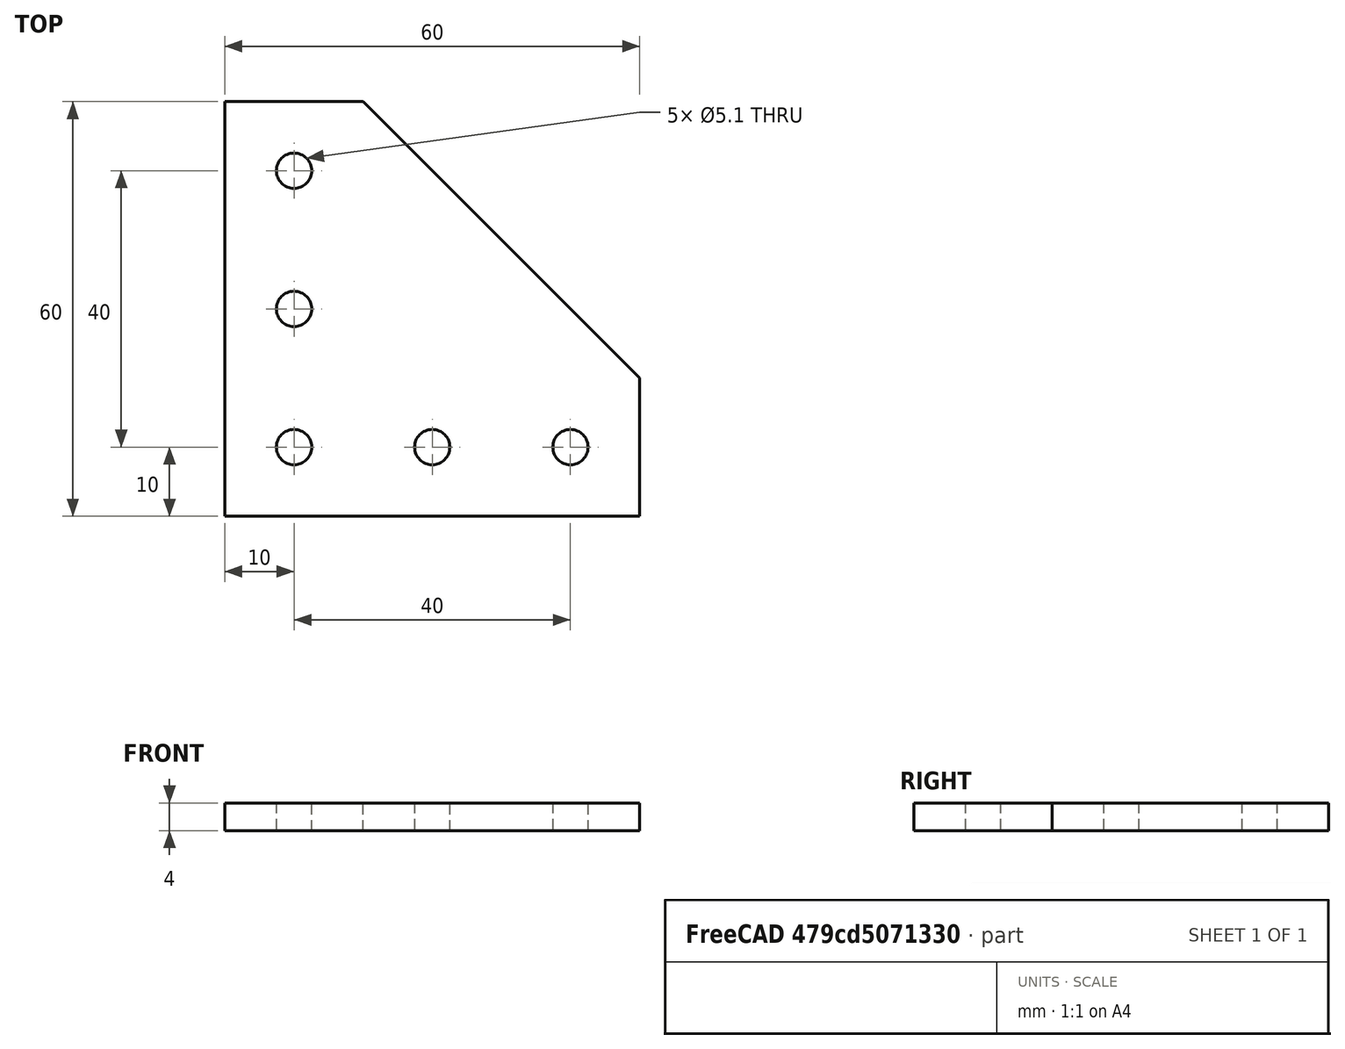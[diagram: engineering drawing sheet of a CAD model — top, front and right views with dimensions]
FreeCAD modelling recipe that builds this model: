
FCSTD DOCUMENT  (FreeCAD 0.20R25645 (Git))
Label: 2020 90deg plate
License: All rights reserved
LicenseURL: http://en.wikipedia.org/wiki/All_rights_reserved
objects: Sketcher::SketchObject×1, PartDesign::Pad×1, PartDesign::Body×1
note: 4 computed .brp shape members not serialized (recipe doc carries the construction recipe); baked Part::Feature solids carry a one-line shape summary decoded from their .brp

FEATURE [Sketcher::SketchObject] Sketch
  FullyConstrained = true
  MapMode = 5
  Support = -> [XY_Plane]
  sketch-geometry (14):
    g0: LineSegment StartX=0 StartY=0 StartZ=0 EndX=0 EndY=60 EndZ=0
    g1: LineSegment StartX=0 StartY=0 StartZ=0 EndX=60 EndY=0 EndZ=0
    g2: LineSegment StartX=0 StartY=60 StartZ=0 EndX=20 EndY=60 EndZ=0
    g3: LineSegment StartX=60 StartY=0 StartZ=0 EndX=60 EndY=20 EndZ=0
    g4: LineSegment StartX=20 StartY=60 StartZ=0 EndX=60 EndY=20 EndZ=0
    g5: Circle CenterX=10 CenterY=10 CenterZ=0 NormalX=0 NormalY=0 NormalZ=1 AngleXU=0 Radius=2.55
    g6: Circle CenterX=30 CenterY=10 CenterZ=0 NormalX=0 NormalY=0 NormalZ=1 AngleXU=0 Radius=2.55
    g7: Circle CenterX=50 CenterY=10 CenterZ=0 NormalX=0 NormalY=0 NormalZ=1 AngleXU=0 Radius=2.55
    g8: LineSegment StartX=10 StartY=10 StartZ=0 EndX=30 EndY=10 EndZ=0
    g9: LineSegment StartX=30 StartY=10 StartZ=0 EndX=50 EndY=10 EndZ=0
    g10: LineSegment StartX=10 StartY=10 StartZ=0 EndX=10 EndY=30 EndZ=0
    g11: LineSegment StartX=10 StartY=30 StartZ=0 EndX=10 EndY=50 EndZ=0
    g12: Circle CenterX=10 CenterY=30 CenterZ=0 NormalX=0 NormalY=0 NormalZ=1 AngleXU=0 Radius=2.55
    g13: Circle CenterX=10 CenterY=50 CenterZ=0 NormalX=0 NormalY=0 NormalZ=1 AngleXU=0 Radius=2.55
  constraints (37):
    c: Coincident(g0,g-1)
    c: PointOnObject(g0,g-2)
    c: Coincident(g1,g0)
    c: PointOnObject(g1,g-1)
    c: DistanceY(g0,g0) = 60
    c: Coincident(g2,g0)
    c: Horizontal(g2)
    c: DistanceX(g2,g2) = 20
    c: Coincident(g3,g1)
    c: Vertical(g3)
    c: Equal(g1,g0)
    c: Equal(g2,g3)
    c: Coincident(g4,g2)
    c: Coincident(g4,g3)
    c: Diameter(g5) = 5.1
    c: DistanceX(g0,g5) = 10
    c: DistanceY(g0,g5) = 10
    c: Equal(g6,g5)
    c: Horizontal(g5,g6)
    c: DistanceX(g5,g6) = 20
    c: Horizontal(g6,g7)
    c: Equal(g6,g7)
    c: Coincident(g8,g5)
    c: Coincident(g8,g6)
    c: Coincident(g9,g6)
    c: Coincident(g9,g7)
    c: Equal(g8,g9)
    c: Coincident(g10,g5)
    c: Vertical(g10)
    c: Coincident(g11,g10)
    c: Vertical(g11)
    c: Equal(g8,g10)
    c: Equal(g8,g11)
    c: Coincident(g12,g10)
    c: Equal(g5,g12)
    c: Coincident(g13,g11)
    c: Equal(g5,g13)
FEATURE [PartDesign::Pad] Pad
  Direction = (0,0,1)
  Length = 4
  Length2 = 100
  Profile = -> Sketch
  Type = 0
FEATURE [PartDesign::Body] Body
  Group = -> [Sketch,Pad]
  Origin = -> Origin
  Tip = -> Pad
